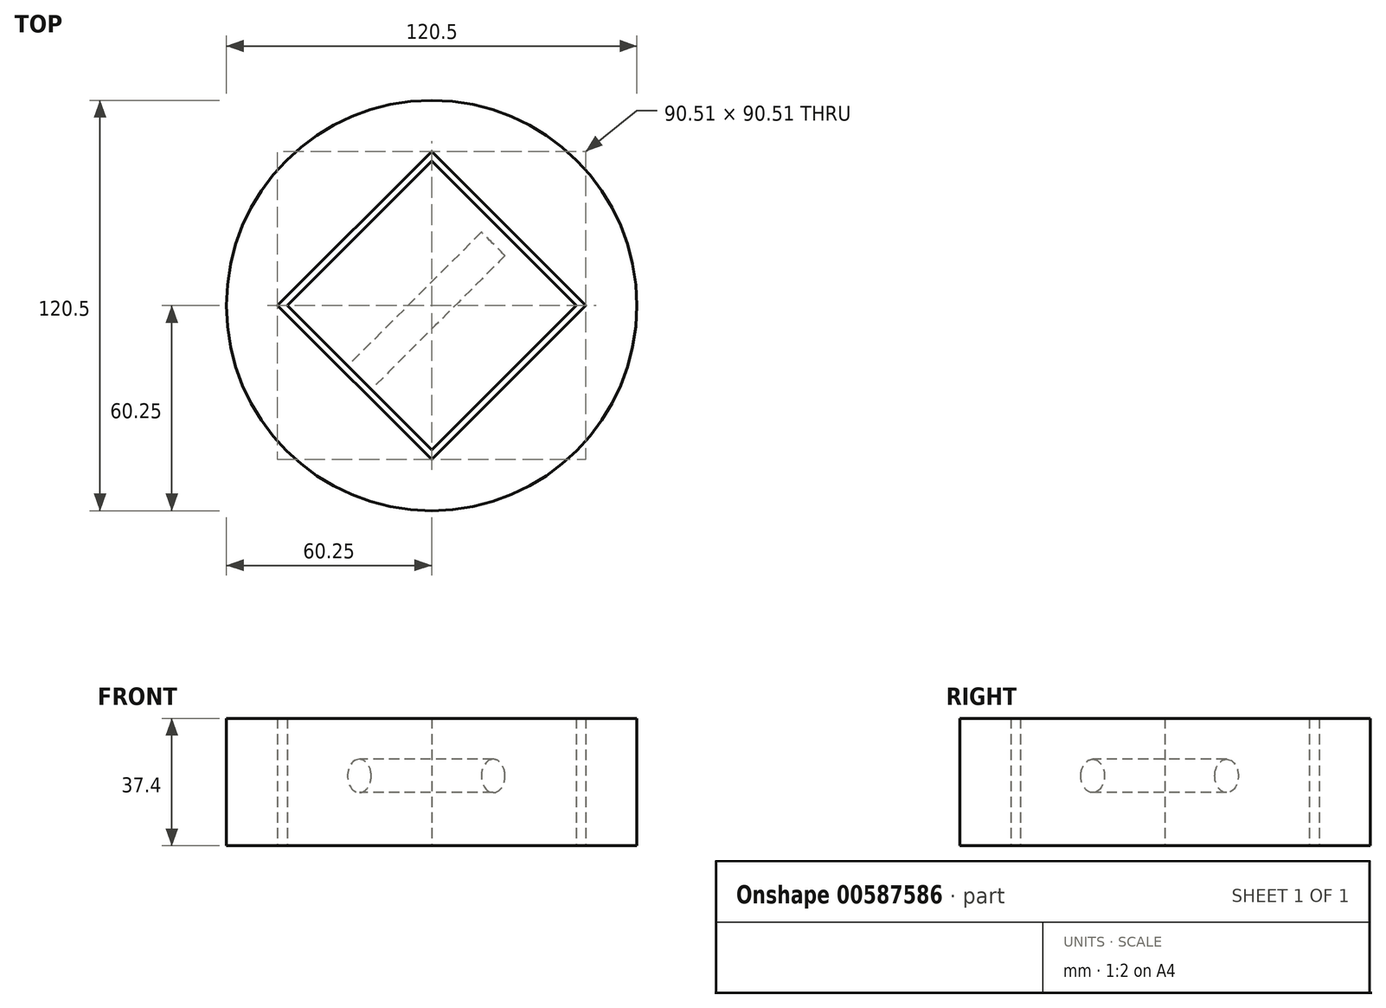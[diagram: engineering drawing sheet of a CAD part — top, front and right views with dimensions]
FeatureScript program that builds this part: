
annotation { "Feature Type Name" : "Feature", "Feature Type Description" : "" }
export const myFeature = defineFeature(function(context is Context, id is Id, definition is map)
    precondition{}
    {
        {
            var Q0;
            Q0=qCreatedBy(makeId("Top.planeOp"),FACE);
            var sketch = newSketch(context, id + "F0", { "sketchPlane" : qUnion([Q0])});
            skLineSegment(sketch, "E0", {"start": v(-42.43, 0) * mm, "end": v(0, 42.43) * mm});
            skLineSegment(sketch, "E1", {"start": v(0, 42.43) * mm, "end": v(42.43, 0) * mm});
            skLineSegment(sketch, "E2", {"start": v(42.43, 0) * mm, "end": v(0, -42.43) * mm});
            skLineSegment(sketch, "E3", {"start": v(0, -42.43) * mm, "end": v(-42.43, 0) * mm});
            skSolve(sketch);
        }
        {
            var Q0;
            Q0=makeQuery(id+"F0.imprint","IMPRINT",FACE,{"disambiguationData":[TD([[makeQuery(id+"F0.imprint","IMPRINT",EDGE,{"derivedFrom":sQuery(id+"F0.wireOp",EDGE,"E0")}),-1.0]])]});
            extrude(context, id + "F1", {"entities" : qUnion([Q0]), "depth" : 37.4 * mm, "offsetDistance" : 25 * mm});
        }
        {
            var Q0;
            Q0=makeQuery(id+"F1.opExtrude","SWEPT_FACE",FACE,{"disambiguationData":[OSD([sQuery(id+"F0.wireOp",EDGE,"E3")])]});
            var sketch = newSketch(context, id + "F2", { "sketchPlane" : qUnion([Q0])});
            skCircle(sketch, "E4", {"center": v(0, 20.52) * mm, "radius": 4.9 * mm});
            skSolve(sketch);
        }
        {
            var Q0;
            Q0 = qSketchRegion(id + "F2", true);
            extrude(context, id + "F3", {"entities" : qUnion([Q0]), "operationType" : NewBodyOperationType.REMOVE, "oppositeDirection" : true, "depth" : 55.6 * mm, "offsetDistance" : 25 * mm});
        }
        {
            var Q0;
            Q0=qCreatedBy(makeId("Top.planeOp"),FACE);
            var sketch = newSketch(context, id + "F4", { "sketchPlane" : qUnion([Q0])});
            skLineSegment(sketch, "E5", {"start": v(0, -45.25) * mm, "end": v(-45.25, 0) * mm});
            skLineSegment(sketch, "E6", {"start": v(-45.25, 0) * mm, "end": v(0, 45.25) * mm});
            skLineSegment(sketch, "E7", {"start": v(0, 45.25) * mm, "end": v(45.25, 0) * mm});
            skLineSegment(sketch, "E8", {"start": v(45.25, 0) * mm, "end": v(0, -45.25) * mm});
            skCircle(sketch, "E9", {"center": v(0, 0) * mm, "radius": 60.25 * mm});
            skSolve(sketch);
        }
        {
            var Q0;
            Q0 = qSketchRegion(id + "F4", true);
            var Q1;
            Q1=makeQuery(id+"F1.opExtrude","CAP_FACE",FACE,{"disambiguationData":[OSD([sQuery(id+"F0.wireOp",EDGE,"E0"),sQuery(id+"F0.wireOp",EDGE,"E1"),sQuery(id+"F0.wireOp",EDGE,"E2"),sQuery(id+"F0.wireOp",EDGE,"E3")])],"isStart":false});
            extrude(context, id + "F5", {"entities" : qUnion([Q0]), "endBound" : BoundingType.UP_TO_SURFACE, "depth" : 31.1 * mm, "endBoundEntityFace" : qUnion([Q1]), "offsetDistance" : 25 * mm});
        }
    });
